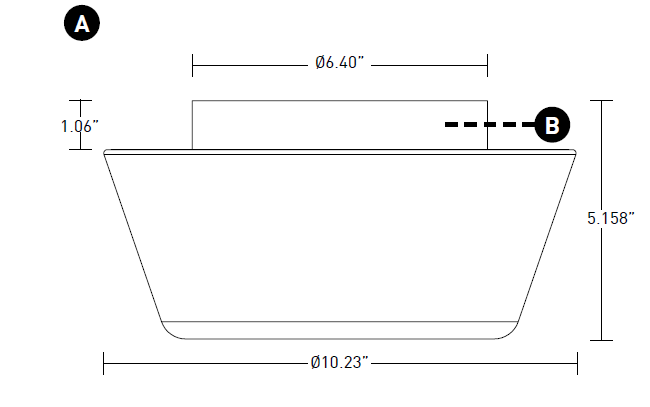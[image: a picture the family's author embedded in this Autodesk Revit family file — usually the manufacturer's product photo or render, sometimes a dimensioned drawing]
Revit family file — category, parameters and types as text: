
# Revit family: Lighting-Accent-Amerlux-WMACCS
name_source: partatom
category: Lighting Fixtures
revit_build: Autodesk Revit 2017 (Build: 20190508_0315(x64)
units: mm (PartAtom-declared; Revit-internal decimal feet)

## family parameters
Cut with Voids When Loaded = No
Host = Face
Light Source = Yes
Part Type = Normal
Room Calculation Point = No
Round Connector Dimension = Use Diameter
Shared = No

## types (1)
- Lighting-Accent-Amerlux-WMACCS
    Apparent Load = 0 VA
    Color Filter = 16777215
    Default Elevation = 48"
    Description = Small Wall Mount Accent
    Dimming Lamp Color Temperature Shift = <None>
    Emit Shape Visible in Rendering = Yes
    Emit from Circle Diameter = 2"
    Lamp = LED
    Manufacturer = Amerlux
    Material = Black Finish
    Model = WMACCS
    Number of Poles = 1
    Photometric Web File = generic
    Power Factor = 1
    Tilt Angle = 45.00°
    URL = http://www.amerlux.com
    Voltage = 0 V

## geometry (parser evidence)
native form markers: Blend x18, Sweep x3
no freeform markers — native parametric forms only
